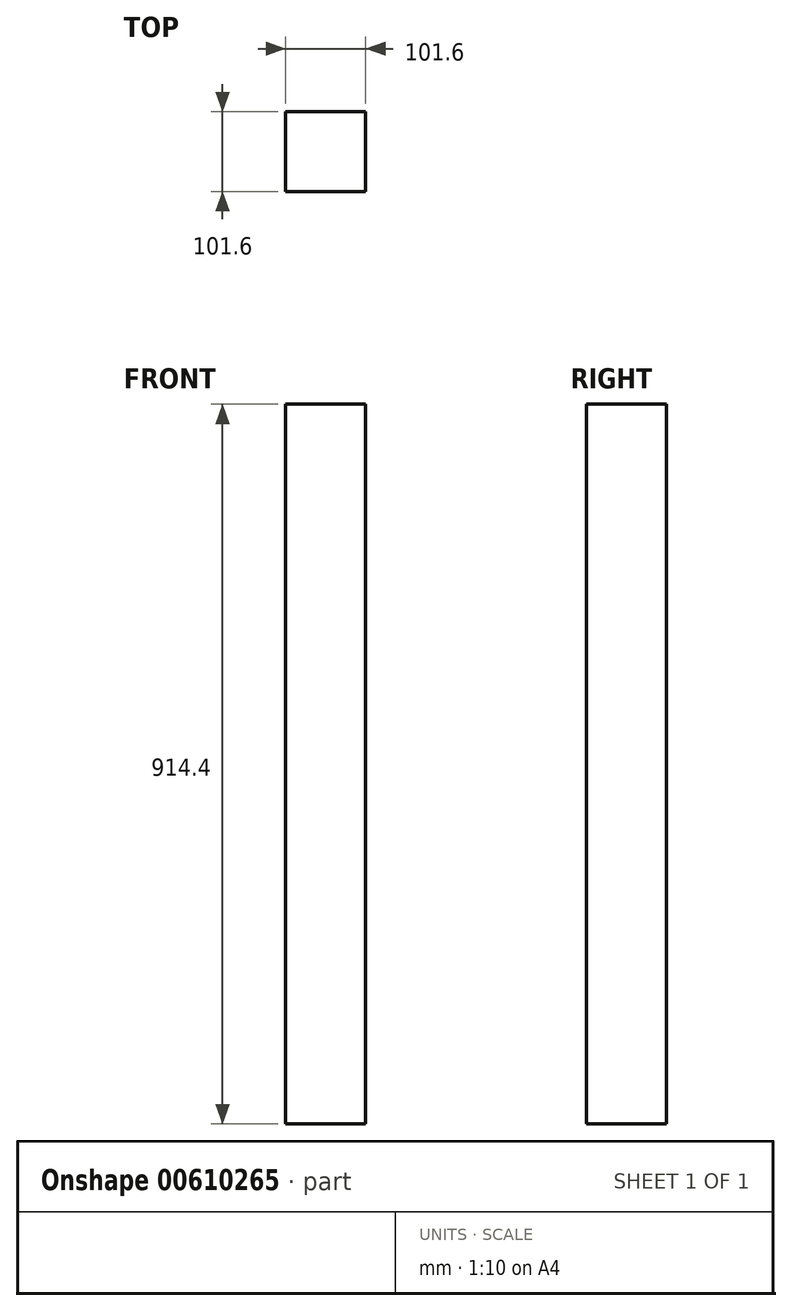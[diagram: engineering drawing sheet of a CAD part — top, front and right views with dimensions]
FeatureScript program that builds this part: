
annotation { "Feature Type Name" : "Feature", "Feature Type Description" : "" }
export const myFeature = defineFeature(function(context is Context, id is Id, definition is map)
    precondition{}
    {
        {
            var Q0;
            Q0=qCreatedBy(makeId("Top.planeOp"),FACE);
            var sketch = newSketch(context, id + "F0", { "sketchPlane" : qUnion([Q0])});
            skLineSegment(sketch, "E0.bottom", {"start": v(-50.8, 50.8) * mm, "end": v(50.8, 50.8) * mm});
            skLineSegment(sketch, "E0.top", {"start": v(-50.8, -50.8) * mm, "end": v(50.8, -50.8) * mm});
            skLineSegment(sketch, "E0.left", {"start": v(-50.8, 50.8) * mm, "end": v(-50.8, -50.8) * mm});
            skLineSegment(sketch, "E0.right", {"start": v(50.8, 50.8) * mm, "end": v(50.8, -50.8) * mm});
            skSolve(sketch);
        }
        {
            var Q0;
            Q0 = qSketchRegion(id + "F0", true);
            extrude(context, id + "F1", {"entities" : qUnion([Q0]), "depth" : 914.4 * mm, "offsetDistance" : 25.4 * mm});
        }
    });
